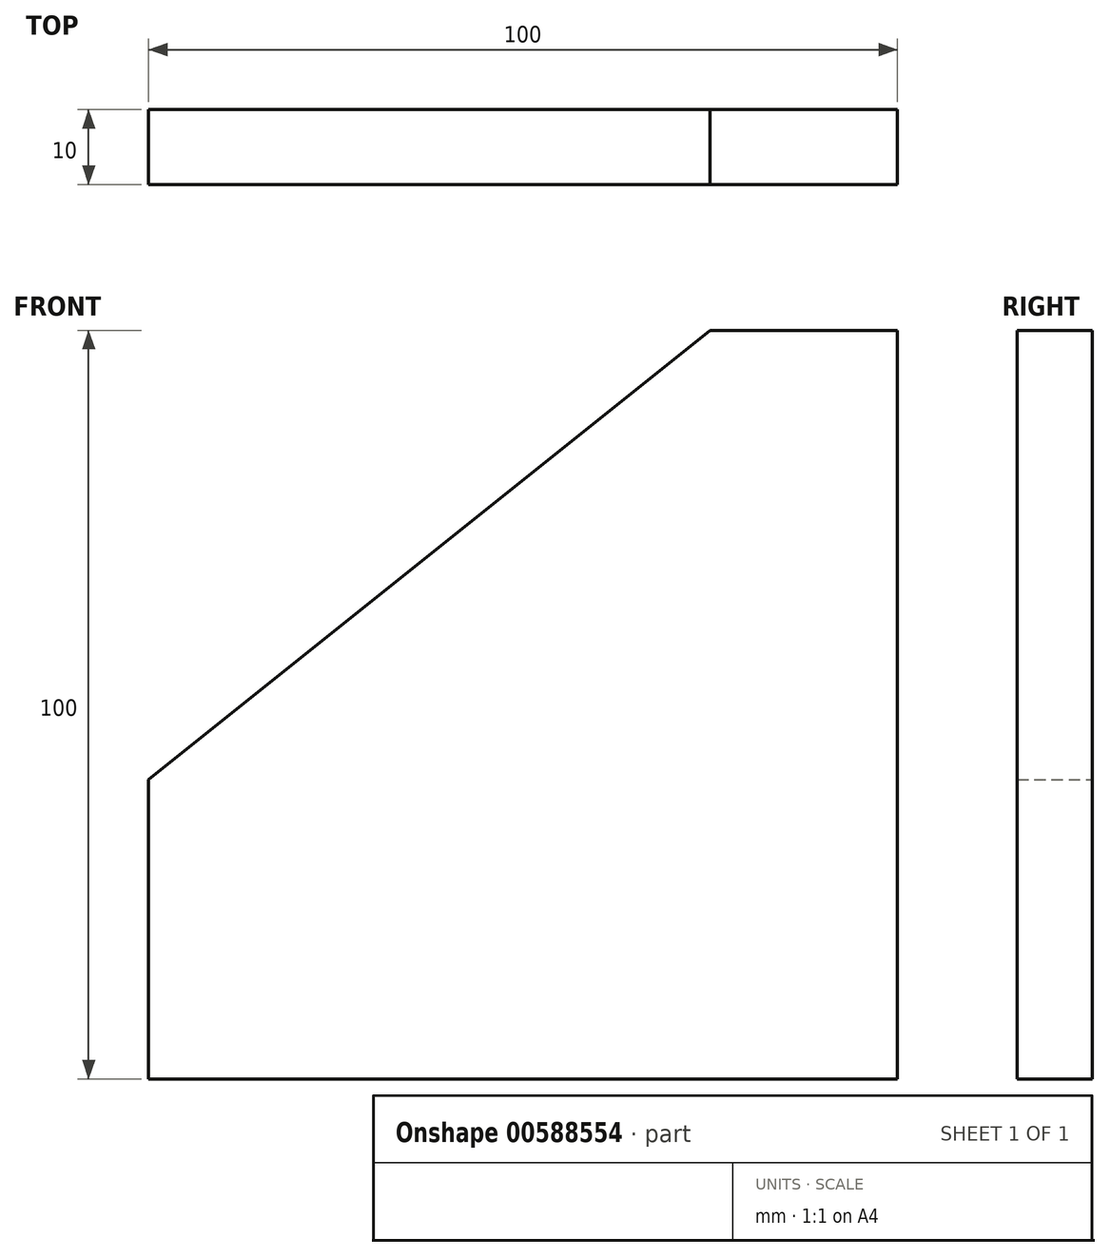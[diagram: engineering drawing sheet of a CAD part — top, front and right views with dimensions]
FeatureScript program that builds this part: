
annotation { "Feature Type Name" : "Feature", "Feature Type Description" : "" }
export const myFeature = defineFeature(function(context is Context, id is Id, definition is map)
    precondition{}
    {
        {
            var Q0;
            Q0=qCreatedBy(makeId("Front.planeOp"),FACE);
            var sketch = newSketch(context, id + "F0", { "sketchPlane" : qUnion([Q0])});
            skLineSegment(sketch, "E0", {"start": v(0, 0) * mm, "end": v(0, 100) * mm});
            skLineSegment(sketch, "E1", {"start": v(0, 100) * mm, "end": v(-25, 100) * mm});
            skLineSegment(sketch, "E2", {"start": v(-25, 100) * mm, "end": v(-100, 40) * mm});
            skLineSegment(sketch, "E3", {"start": v(-100, 40) * mm, "end": v(-100, 0) * mm});
            skLineSegment(sketch, "E4", {"start": v(-100, 0) * mm, "end": v(0, 0) * mm});
            skSolve(sketch);
        }
        {
            var Q0;
            Q0=makeQuery(id+"F0.imprint","IMPRINT",FACE,{"disambiguationData":[TD([[makeQuery(id+"F0.imprint","IMPRINT",EDGE,{"derivedFrom":sQuery(id+"F0.wireOp",EDGE,"E0")}),1.0]])]});
            extrude(context, id + "F1", {"entities" : qUnion([Q0]), "depth" : 10 * mm, "offsetDistance" : 25 * mm});
        }
    });
